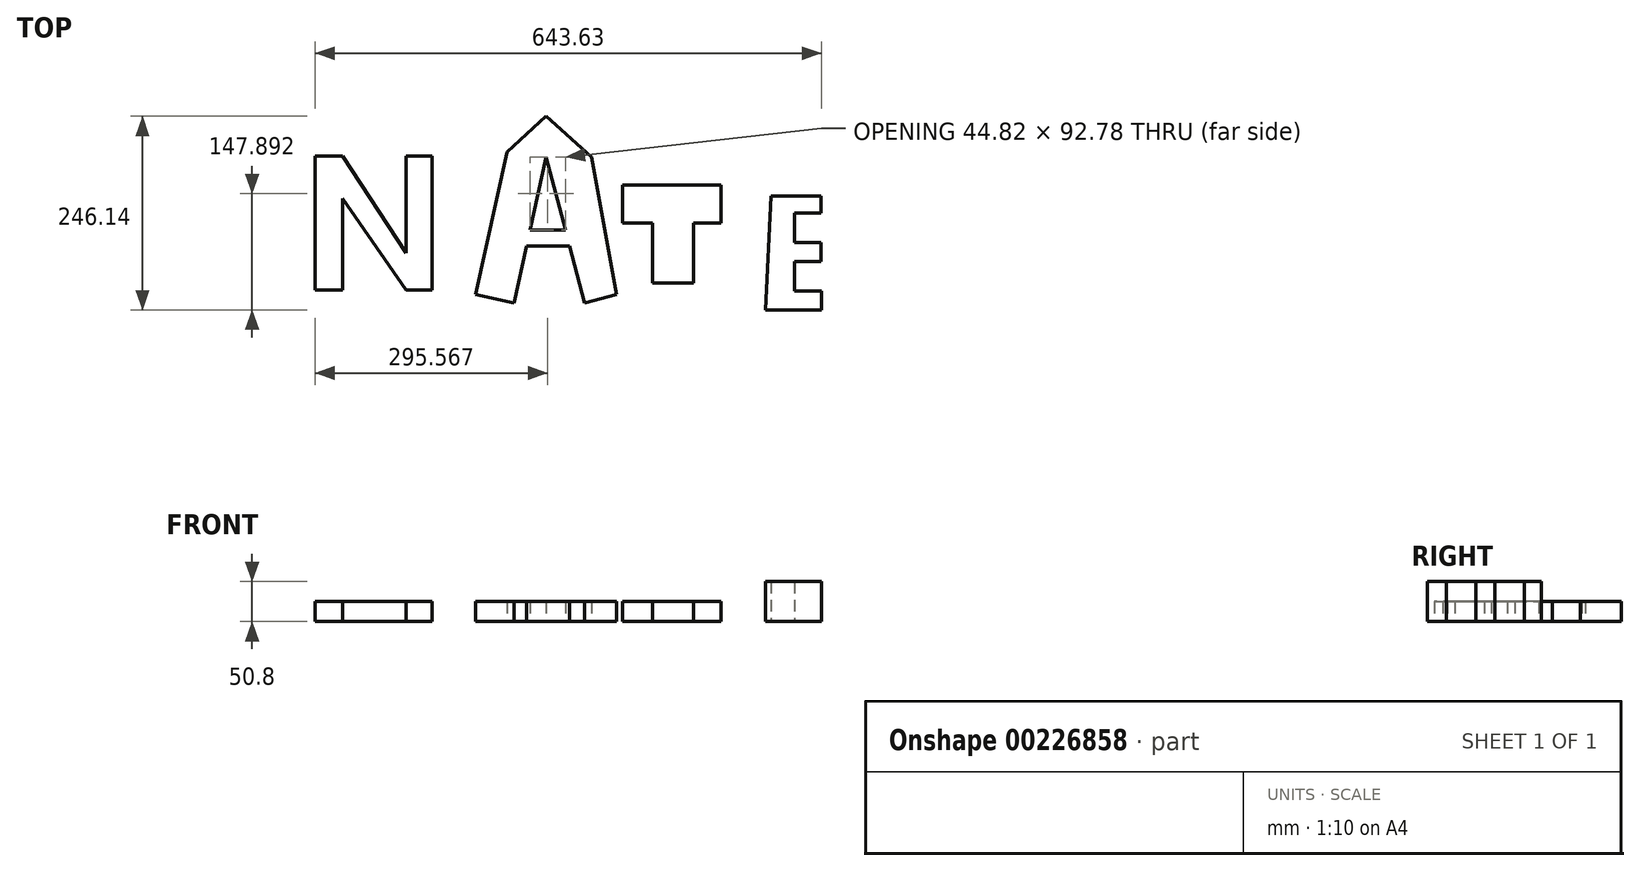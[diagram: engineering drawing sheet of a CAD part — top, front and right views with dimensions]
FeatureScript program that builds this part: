
annotation { "Feature Type Name" : "Feature", "Feature Type Description" : "" }
export const myFeature = defineFeature(function(context is Context, id is Id, definition is map)
    precondition{}
    {
        {
            var Q0;
            Q0=qCreatedBy(makeId("Top.planeOp"),FACE);
            var sketch = newSketch(context, id + "F0", { "sketchPlane" : qUnion([Q0])});
            skLineSegment(sketch, "E0.bottom", {"start": v(-217.55, 85.06) * mm, "end": v(-182.45, 85.06) * mm});
            skLineSegment(sketch, "E0.top", {"start": v(-217.55, -85.66) * mm, "end": v(-182.45, -85.66) * mm});
            skLineSegment(sketch, "E0.left", {"start": v(-217.55, 85.06) * mm, "end": v(-217.55, -85.66) * mm});
            skLineSegment(sketch, "E0.right", {"start": v(-182.45, 85.06) * mm, "end": v(-182.45, -85.66) * mm});
            skLineSegment(sketch, "E1.bottom", {"start": v(-101.84, 85.06) * mm, "end": v(-68.64, 85.06) * mm});
            skLineSegment(sketch, "E1.top", {"start": v(-101.84, -85.66) * mm, "end": v(-68.64, -85.66) * mm});
            skLineSegment(sketch, "E1.left", {"start": v(-101.84, 85.06) * mm, "end": v(-101.84, -85.66) * mm});
            skLineSegment(sketch, "E1.right", {"start": v(-68.64, 85.06) * mm, "end": v(-68.64, -85.66) * mm});
            skLineSegment(sketch, "E2", {"start": v(-182.45, 85.06) * mm, "end": v(-101.84, -38.24) * mm});
            skLineSegment(sketch, "E3", {"start": v(-101.84, -38.24) * mm, "end": v(-101.84, -85.66) * mm});
            skLineSegment(sketch, "E4", {"start": v(-101.84, -85.66) * mm, "end": v(-182.45, 31) * mm});
            skLineSegment(sketch, "E5", {"start": v(26.2, 89.8) * mm, "end": v(-13.63, -91.35) * mm});
            skLineSegment(sketch, "E6", {"start": v(-13.63, -91.35) * mm, "end": v(35.2, -102.09) * mm});
            skLineSegment(sketch, "E7", {"start": v(35.2, -102.09) * mm, "end": v(76, 83.47) * mm});
            skLineSegment(sketch, "E8", {"start": v(76, 83.47) * mm, "end": v(124.84, -102.09) * mm});
            skLineSegment(sketch, "E9", {"start": v(124.84, -102.09) * mm, "end": v(165.65, -91.35) * mm});
            skLineSegment(sketch, "E10", {"start": v(165.65, -91.35) * mm, "end": v(133.38, 83.47) * mm});
            skLineSegment(sketch, "E11", {"start": v(55.6, -9.3) * mm, "end": v(100.43, -9.3) * mm});
            skLineSegment(sketch, "E12", {"start": v(51.11, -29.76) * mm, "end": v(105.8, -29.76) * mm});
            skLineSegment(sketch, "E13", {"start": v(26.2, 89.8) * mm, "end": v(76, 135.33) * mm});
            skLineSegment(sketch, "E14", {"start": v(133.38, 83.47) * mm, "end": v(76, 135.33) * mm});
            skLineSegment(sketch, "E15", {"start": v(214, 115.4) * mm, "end": v(214, 48.07) * mm});
            skLineSegment(sketch, "E16", {"start": v(211.15, 0) * mm, "end": v(211.15, -76.18) * mm});
            skLineSegment(sketch, "E17", {"start": v(211.15, -76.18) * mm, "end": v(263.32, -76.18) * mm});
            skLineSegment(sketch, "E18", {"start": v(263.32, -76.18) * mm, "end": v(263.32, 0) * mm});
            skLineSegment(sketch, "E19", {"start": v(263.32, 49.97) * mm, "end": v(263.32, 116.36) * mm});
            skLineSegment(sketch, "E20", {"start": v(214, 115.4) * mm, "end": v(263.32, 116.36) * mm});
            skLineSegment(sketch, "E21", {"start": v(173.21, 48.07) * mm, "end": v(173.21, 0) * mm});
            skLineSegment(sketch, "E22", {"start": v(298.4, 48.07) * mm, "end": v(298.4, 0) * mm});
            skLineSegment(sketch, "E23", {"start": v(173.21, 48.07) * mm, "end": v(298.4, 48.07) * mm});
            skLineSegment(sketch, "E24", {"start": v(173.21, 0) * mm, "end": v(298.4, 0) * mm});
            skLineSegment(sketch, "E25", {"start": v(369.54, 38.59) * mm, "end": v(486.2, 38.59) * mm});
            skLineSegment(sketch, "E26", {"start": v(486.2, 38.59) * mm, "end": v(486.2, 115.4) * mm});
            skLineSegment(sketch, "E27", {"start": v(486.2, 115.4) * mm, "end": v(371.44, 115.4) * mm});
            skLineSegment(sketch, "E28", {"start": v(371.44, 115.4) * mm, "end": v(371.44, -30.65) * mm});
            skLineSegment(sketch, "E29", {"start": v(371.44, -30.65) * mm, "end": v(498.53, -30.65) * mm});
            skSolve(sketch);
        }
        {
            var Q0;
            Q0 = qSketchRegion(id + "F0", true);
            extrude(context, id + "F1", {"entities" : qUnion([Q0]), "depth" : 25.4 * mm});
        }
        {
            var Q0;
            Q0=makeQuery(id+"F1.opExtrude","CAP_FACE",FACE,{"disambiguationData":[OSD([sQuery(id+"F0.wireOp",EDGE,"E25"),sQuery(id+"F0.wireOp",EDGE,"E26"),sQuery(id+"F0.wireOp",EDGE,"E27"),sQuery(id+"F0.wireOp",EDGE,"E28")])],"isStart":false});
            var sketch = newSketch(context, id + "F2", { "sketchPlane" : qUnion([Q0])});
            skLineSegment(sketch, "E30", {"start": v(371.44, 38.59) * mm, "end": v(371.44, -18.32) * mm});
            skLineSegment(sketch, "E31", {"start": v(371.44, -18.32) * mm, "end": v(487.15, -18.32) * mm});
            skLineSegment(sketch, "E32", {"start": v(487.15, -18.32) * mm, "end": v(487.15, 0) * mm});
            skLineSegment(sketch, "E33", {"start": v(487.15, 0) * mm, "end": v(395.15, 0) * mm});
            skLineSegment(sketch, "E34", {"start": v(395.15, 0) * mm, "end": v(395.15, 38.59) * mm});
            skSolve(sketch);
        }
        {
            var Q0;
            {var subQ0=sQuery(id+"F2.wireOp",EDGE,"E30");Q0=makeQuery(id+"F2.imprint","IMPRINT",FACE,{"disambiguationData":[TD([[makeQuery(id+"F2.imprint","IMPRINT",EDGE,{"derivedFrom":subQ0}),1.0]])]});}
            extrude(context, id + "F3", {"entities" : qUnion([Q0]), "depth" : 50.8 * mm});
        }
        {
            var Q0;
            Q0=makeQuery(id+"F1.opExtrude","CAP_FACE",FACE,{"disambiguationData":[OSD([sQuery(id+"F0.wireOp",EDGE,"E25"),sQuery(id+"F0.wireOp",EDGE,"E26"),sQuery(id+"F0.wireOp",EDGE,"E27"),sQuery(id+"F0.wireOp",EDGE,"E28")])],"isStart":false});
            var sketch = newSketch(context, id + "F4", { "sketchPlane" : qUnion([Q0])});
            skLineSegment(sketch, "E35.bottom", {"start": v(417.91, 84.11) * mm, "end": v(449.21, 84.11) * mm});
            skLineSegment(sketch, "E35.top", {"start": v(417.91, 60.4) * mm, "end": v(449.21, 60.4) * mm});
            skLineSegment(sketch, "E35.left", {"start": v(417.91, 84.11) * mm, "end": v(417.91, 60.4) * mm});
            skLineSegment(sketch, "E35.right", {"start": v(449.21, 84.11) * mm, "end": v(449.21, 60.4) * mm});
            skSolve(sketch);
        }
        {
            var Q0;
            Q0=makeQuery(id+"F4.imprint","IMPRINT",FACE,{"disambiguationData":[TD([[makeQuery(id+"F4.imprint","IMPRINT",EDGE,{"derivedFrom":sQuery(id+"F4.wireOp",EDGE,"E35.bottom")}),-1.0]])]});
            extrude(context, id + "F5", {"entities" : qUnion([Q0]), "operationType" : NewBodyOperationType.REMOVE, "oppositeDirection" : true, "depth" : 50.8 * mm});
        }
        {
            var Q0;
            Q0=makeQuery(id+"F3.opExtrude","SWEPT_FACE",FACE,{"disambiguationData":[OSD([sQuery(id+"F0.wireOp",EDGE,"E25")])]});
            extrude(context, id + "F6", {"entities" : qUnion([Q0]), "operationType" : NewBodyOperationType.REMOVE, "oppositeDirection" : true, "depth" : 25.4 * mm});
        }
        {
            var Q0;
            Q0=makeQuery(id+"F6.boolean.opBoolean","COPY",FACE,{"derivedFrom":makeQuery(id+"F6.opExtrude","CAP_FACE",FACE,{"disambiguationData":[OSD([sQuery(id+"F0.wireOp",EDGE,"E25")])],"isStart":false})});
            extrude(context, id + "F7", {"entities" : qUnion([Q0]), "operationType" : NewBodyOperationType.REMOVE, "oppositeDirection" : true, "depth" : 25.4 * mm});
        }
        {
            var Q0;
            Q0=makeQuery(id+"F3.opExtrude","SWEPT_FACE",FACE,{"disambiguationData":[OSD([sQuery(id+"F2.wireOp",EDGE,"E33")])]});
            extrude(context, id + "F8", {"entities" : qUnion([Q0]), "operationType" : NewBodyOperationType.REMOVE, "oppositeDirection" : true, "depth" : 25.4 * mm});
        }
        {
            var Q0;
            Q0=makeQuery(id+"F7.boolean.opBoolean","COPY",FACE,{"derivedFrom":makeQuery(id+"F7.opExtrude","CAP_FACE",FACE,{"disambiguationData":[OSD([sQuery(id+"F0.wireOp",EDGE,"E25")])],"isStart":false})});
            extrude(context, id + "F9", {"entities" : qUnion([Q0]), "operationType" : NewBodyOperationType.REMOVE, "oppositeDirection" : true, "depth" : 25.4 * mm});
        }
        {
            var Q0;
            Q0=makeQuery(id+"F1.opExtrude","CAP_FACE",FACE,{"disambiguationData":[OSD([sQuery(id+"F0.wireOp",EDGE,"E25"),sQuery(id+"F0.wireOp",EDGE,"E26"),sQuery(id+"F0.wireOp",EDGE,"E27"),sQuery(id+"F0.wireOp",EDGE,"E28")])],"isStart":false});
            extrude(context, id + "F10", {"entities" : qUnion([Q0]), "operationType" : NewBodyOperationType.REMOVE, "oppositeDirection" : true, "depth" : 25.4 * mm});
        }
        {
            var Q0;
            Q0=qCreatedBy(makeId("Top.planeOp"),FACE);
            var sketch = newSketch(context, id + "F11", { "sketchPlane" : qUnion([Q0])});
            skLineSegment(sketch, "E36", {"start": v(361.35, 33.88) * mm, "end": v(425.44, 33.88) * mm});
            skLineSegment(sketch, "E37", {"start": v(425.44, 33.88) * mm, "end": v(425.44, 12.3) * mm});
            skLineSegment(sketch, "E38", {"start": v(425.44, 12.3) * mm, "end": v(391.81, 12.3) * mm});
            skLineSegment(sketch, "E39", {"start": v(391.81, 12.3) * mm, "end": v(391.81, -25.14) * mm});
            skLineSegment(sketch, "E40", {"start": v(391.81, -25.14) * mm, "end": v(425.44, -25.14) * mm});
            skLineSegment(sketch, "E41", {"start": v(425.44, -25.14) * mm, "end": v(425.44, -49.25) * mm});
            skLineSegment(sketch, "E42", {"start": v(425.44, -49.25) * mm, "end": v(391.81, -49.25) * mm});
            skLineSegment(sketch, "E43", {"start": v(391.81, -49.25) * mm, "end": v(391.81, -86.7) * mm});
            skLineSegment(sketch, "E44", {"start": v(391.81, -86.7) * mm, "end": v(426.08, -86.7) * mm});
            skLineSegment(sketch, "E45", {"start": v(426.08, -86.7) * mm, "end": v(426.08, -110.8) * mm});
            skLineSegment(sketch, "E46", {"start": v(426.08, -110.8) * mm, "end": v(354.37, -110.8) * mm});
            skLineSegment(sketch, "E47", {"start": v(354.37, -110.8) * mm, "end": v(361.35, 33.88) * mm});
            skSolve(sketch);
        }
        {
            var Q0;
            Q0=makeQuery(id+"F11.imprint","IMPRINT",FACE,{"disambiguationData":[TD([[makeQuery(id+"F11.imprint","IMPRINT",EDGE,{"derivedFrom":sQuery(id+"F11.wireOp",EDGE,"E36")}),-1.0]])]});
            extrude(context, id + "F12", {"entities" : qUnion([Q0]), "depth" : 50.8 * mm});
        }
    });
